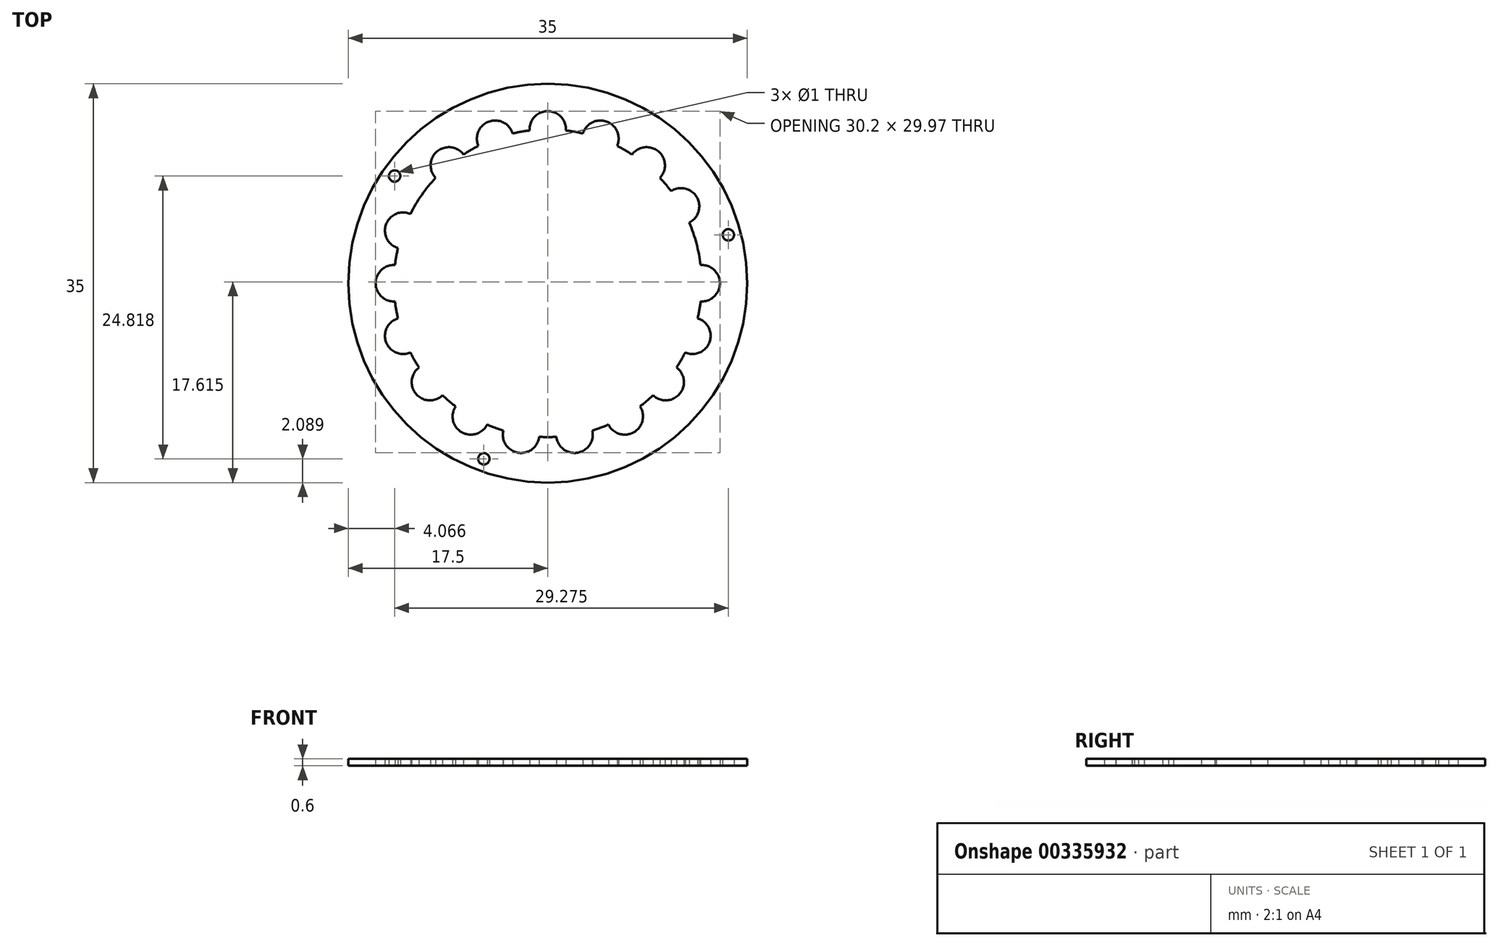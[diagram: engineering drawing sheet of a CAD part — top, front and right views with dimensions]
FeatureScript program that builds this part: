
annotation { "Feature Type Name" : "Feature", "Feature Type Description" : "" }
export const myFeature = defineFeature(function(context is Context, id is Id, definition is map)
    precondition{}
    {
        {
            var Q0;
            Q0=qCreatedBy(makeId("Top.planeOp"),FACE);
            var sketch = newSketch(context, id + "F0", { "sketchPlane" : qUnion([Q0])});
            skCircle(sketch, "E0", {"center": v(0, 0) * mm, "radius": 17.5 * mm});
            skLineSegment(sketch, "E1", {"start": v(0, 0) * mm, "end": v(15.84, 4.24) * mm, "construction": true});
            skLineSegment(sketch, "E2", {"start": v(0, 0) * mm, "end": v(-5.6, -15.41) * mm, "construction": true});
            skLineSegment(sketch, "E3", {"start": v(0, 0) * mm, "end": v(-13.43, 9.4) * mm, "construction": true});
            skCircle(sketch, "E4", {"center": v(15.84, 4.24) * mm, "radius": 0.5 * mm});
            skCircle(sketch, "E5", {"center": v(-5.6, -15.41) * mm, "radius": 0.5 * mm});
            skCircle(sketch, "E6", {"center": v(-13.43, 9.4) * mm, "radius": 0.5 * mm});
            skCircle(sketch, "E7", {"center": v(0, 0) * mm, "radius": 13.5 * mm, "construction": true});
            skArc(sketch, "E8", {"start": v(13.4, 1.6) * mm, "mid": v(15.1, 0) * mm, "end": v(13.4, -1.6) * mm});
            skArc(sketch, "E9.1.0", {"start": v(13.14, -3.08) * mm, "mid": v(14.19, -5.16) * mm, "end": v(12.05, -6.09) * mm});
            skArc(sketch, "E9.2.0", {"start": v(11.3, -7.4) * mm, "mid": v(11.57, -9.7) * mm, "end": v(9.24, -9.84) * mm});
            skArc(sketch, "E9.3.0", {"start": v(8.09, -10.81) * mm, "mid": v(7.55, -13.08) * mm, "end": v(5.32, -12.4) * mm});
            skArc(sketch, "E9.4.0", {"start": v(3.9, -12.92) * mm, "mid": v(2.62, -14.87) * mm, "end": v(0.75, -13.48) * mm});
            skArc(sketch, "E9.5.0", {"start": v(-0.75, -13.48) * mm, "mid": v(-2.62, -14.87) * mm, "end": v(-3.9, -12.92) * mm});
            skArc(sketch, "E9.6.0", {"start": v(-5.32, -12.4) * mm, "mid": v(-7.55, -13.08) * mm, "end": v(-8.09, -10.81) * mm});
            skArc(sketch, "E9.7.0", {"start": v(-9.24, -9.84) * mm, "mid": v(-11.57, -9.7) * mm, "end": v(-11.3, -7.4) * mm});
            skArc(sketch, "E9.8.0", {"start": v(-12.05, -6.09) * mm, "mid": v(-14.19, -5.16) * mm, "end": v(-13.14, -3.08) * mm});
            skArc(sketch, "E9.9.0", {"start": v(-13.4, -1.6) * mm, "mid": v(-15.1, 0) * mm, "end": v(-13.4, 1.6) * mm});
            skArc(sketch, "E9.10.0", {"start": v(-13.14, 3.08) * mm, "mid": v(-14.19, 5.16) * mm, "end": v(-12.05, 6.09) * mm});
            skLineSegment(sketch, "E9.anchor1", {"start": v(0, 0) * mm, "end": v(13.4, -1.6) * mm, "construction": true});
            skLineSegment(sketch, "E9.anchor2", {"start": v(0, 0) * mm, "end": v(-12.05, 6.09) * mm, "construction": true});
            skLineSegment(sketch, "E10", {"start": v(0, 0) * mm, "end": v(-8.68, 10.34) * mm, "construction": true});
            skArc(sketch, "E11", {"start": v(-9.84, 9.24) * mm, "mid": v(-9.7, 11.57) * mm, "end": v(-7.4, 11.3) * mm});
            skArc(sketch, "E12.1.0", {"start": v(-6.09, 12.05) * mm, "mid": v(-5.16, 14.19) * mm, "end": v(-3.08, 13.14) * mm});
            skArc(sketch, "E12.2.0", {"start": v(-1.6, 13.4) * mm, "mid": v(0, 15.1) * mm, "end": v(1.6, 13.4) * mm});
            skArc(sketch, "E12.3.0", {"start": v(3.08, 13.14) * mm, "mid": v(5.16, 14.19) * mm, "end": v(6.09, 12.05) * mm});
            skArc(sketch, "E12.4.0", {"start": v(7.4, 11.3) * mm, "mid": v(9.7, 11.57) * mm, "end": v(9.84, 9.24) * mm});
            skArc(sketch, "E12.5.0", {"start": v(10.81, 8.09) * mm, "mid": v(13.08, 7.55) * mm, "end": v(12.4, 5.32) * mm});
            skLineSegment(sketch, "E12.anchor1", {"start": v(0, 0) * mm, "end": v(-9.84, 9.24) * mm, "construction": true});
            skLineSegment(sketch, "E12.anchor2", {"start": v(0, 0) * mm, "end": v(10.81, 8.09) * mm, "construction": true});
            skArc(sketch, "E13", {"start": v(12.4, 5.32) * mm, "mid": v(13.04, 3.5) * mm, "end": v(13.4, 1.6) * mm});
            skArc(sketch, "E14", {"start": v(13.4, -1.6) * mm, "mid": v(13.3, -2.34) * mm, "end": v(13.14, -3.08) * mm});
            skArc(sketch, "E15", {"start": v(12.05, -6.09) * mm, "mid": v(11.7, -6.75) * mm, "end": v(11.3, -7.4) * mm});
            skArc(sketch, "E16", {"start": v(9.24, -9.84) * mm, "mid": v(8.68, -10.34) * mm, "end": v(8.09, -10.81) * mm});
            skArc(sketch, "E17", {"start": v(5.32, -12.4) * mm, "mid": v(4.62, -12.69) * mm, "end": v(3.9, -12.92) * mm});
            skArc(sketch, "E18", {"start": v(0.75, -13.48) * mm, "mid": v(0, -13.5) * mm, "end": v(-0.75, -13.48) * mm});
            skArc(sketch, "E19", {"start": v(-3.9, -12.92) * mm, "mid": v(-4.62, -12.69) * mm, "end": v(-5.32, -12.4) * mm});
            skArc(sketch, "E20", {"start": v(-8.09, -10.81) * mm, "mid": v(-8.68, -10.34) * mm, "end": v(-9.24, -9.84) * mm});
            skArc(sketch, "E21", {"start": v(-11.3, -7.4) * mm, "mid": v(-11.7, -6.75) * mm, "end": v(-12.05, -6.09) * mm});
            skArc(sketch, "E22", {"start": v(-13.14, -3.08) * mm, "mid": v(-13.3, -2.34) * mm, "end": v(-13.4, -1.6) * mm});
            skArc(sketch, "E23", {"start": v(-13.4, 1.6) * mm, "mid": v(-13.3, 2.34) * mm, "end": v(-13.14, 3.08) * mm});
            skArc(sketch, "E24", {"start": v(-12.05, 6.09) * mm, "mid": v(-11.06, 7.74) * mm, "end": v(-9.84, 9.24) * mm});
            skArc(sketch, "E25", {"start": v(-7.4, 11.3) * mm, "mid": v(-6.75, 11.7) * mm, "end": v(-6.09, 12.05) * mm});
            skArc(sketch, "E26", {"start": v(-3.08, 13.14) * mm, "mid": v(-2.34, 13.3) * mm, "end": v(-1.6, 13.4) * mm});
            skArc(sketch, "E27", {"start": v(1.6, 13.4) * mm, "mid": v(2.34, 13.3) * mm, "end": v(3.08, 13.14) * mm});
            skArc(sketch, "E28", {"start": v(6.09, 12.05) * mm, "mid": v(6.75, 11.7) * mm, "end": v(7.4, 11.3) * mm});
            skArc(sketch, "E29", {"start": v(9.84, 9.24) * mm, "mid": v(10.34, 8.68) * mm, "end": v(10.81, 8.09) * mm});
            skSolve(sketch);
        }
        {
            var Q0;
            Q0 = qSketchRegion(id + "F0", true);
            extrude(context, id + "F1", {"entities" : qUnion([Q0]), "depth" : 0.6 * mm});
        }
    });
